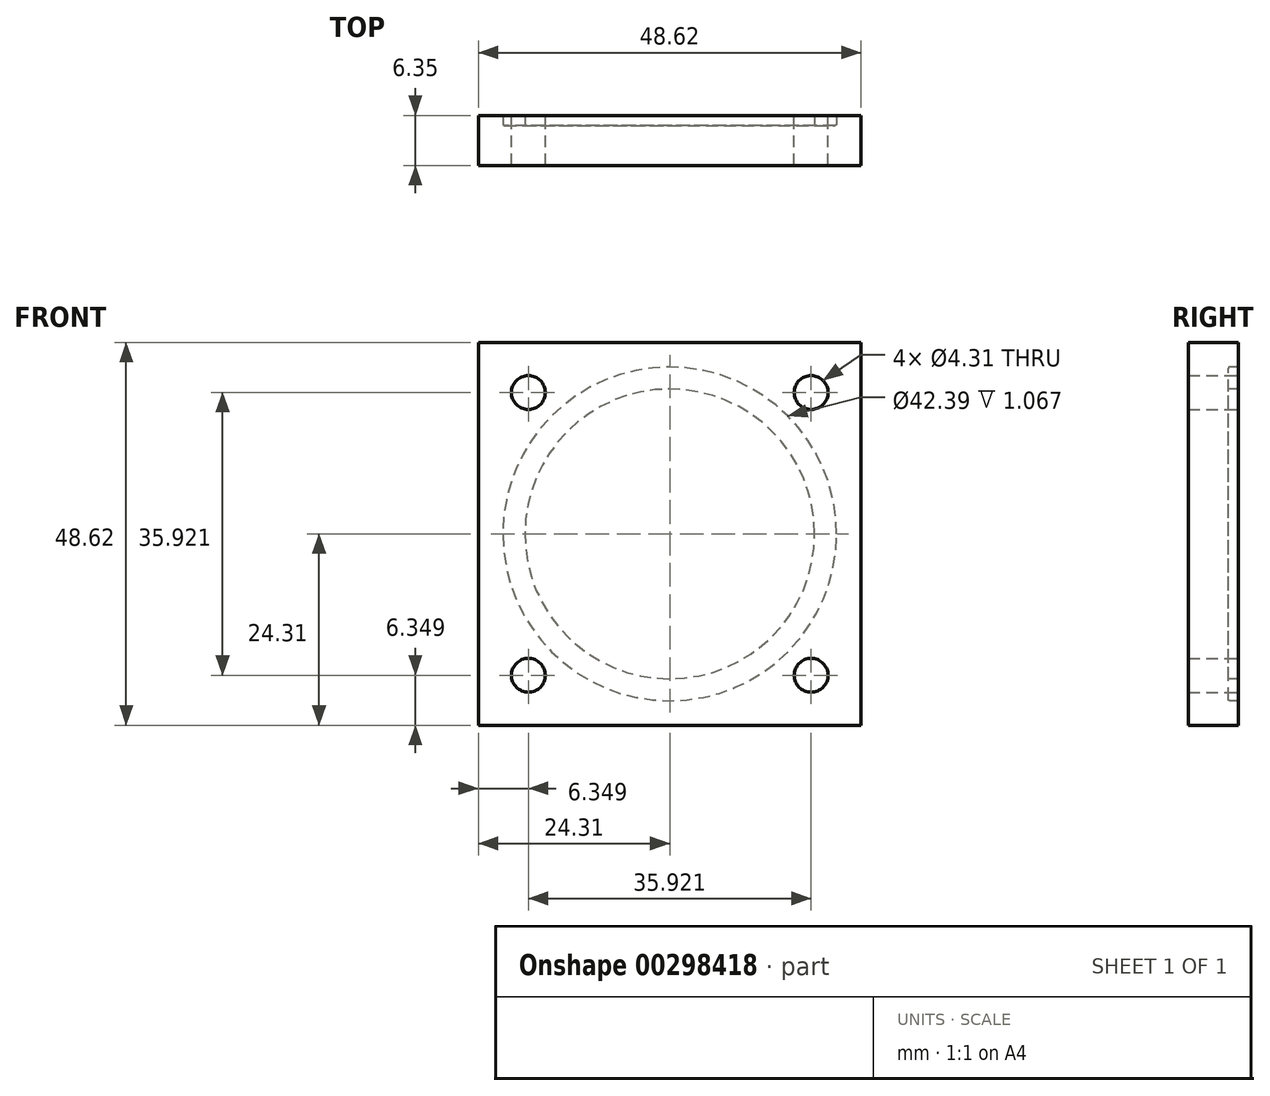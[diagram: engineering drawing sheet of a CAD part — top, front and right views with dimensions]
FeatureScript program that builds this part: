
annotation { "Feature Type Name" : "Feature", "Feature Type Description" : "" }
export const myFeature = defineFeature(function(context is Context, id is Id, definition is map)
    precondition{}
    {
        {
            var Q0;
            Q0=qCreatedBy(makeId("Front.planeOp"),FACE);
            var sketch = newSketch(context, id + "F0", { "sketchPlane" : qUnion([Q0])});
            skLineSegment(sketch, "E0.bottom", {"start": v(24.31, 24.31) * mm, "end": v(-24.31, 24.31) * mm});
            skLineSegment(sketch, "E0.top", {"start": v(24.31, -24.31) * mm, "end": v(-24.31, -24.31) * mm});
            skLineSegment(sketch, "E0.left", {"start": v(24.31, 24.31) * mm, "end": v(24.31, -24.31) * mm});
            skLineSegment(sketch, "E0.right", {"start": v(-24.31, 24.31) * mm, "end": v(-24.31, -24.31) * mm});
            skPoint(sketch, "E0.middle", {"position": v(0, 0) * mm});
            skCircle(sketch, "E1", {"center": v(-17.96, -17.96) * mm, "radius": 2.15 * mm});
            skCircle(sketch, "E2", {"center": v(0, 0) * mm, "radius": 25.4 * mm, "construction": true});
            skLineSegment(sketch, "E3", {"start": v(-17.96, -17.96) * mm, "end": v(0, 0) * mm, "construction": true});
            skCircle(sketch, "E4.1.0", {"center": v(17.96, -17.96) * mm, "radius": 2.15 * mm});
            skCircle(sketch, "E4.2.0", {"center": v(17.96, 17.96) * mm, "radius": 2.15 * mm});
            skCircle(sketch, "E4.3.0", {"center": v(-17.96, 17.96) * mm, "radius": 2.15 * mm});
            skSolve(sketch);
        }
        {
            var Q0;
            Q0=makeQuery(id+"F0.imprint","IMPRINT",FACE,{"disambiguationData":[TD([[makeQuery(id+"F0.imprint","IMPRINT",EDGE,{"derivedFrom":makeQuery(id+"FBOyUSbzv9L5WvW_0.merge.FRwLIMHdycvGu99_1.1.FLy9HZHc7Aeuiqs_1.boolean.opBoolean","COPY",EDGE,{"derivedFrom":makeQuery(id+"FBOyUSbzv9L5WvW_0.merge.FRwLIMHdycvGu99_1.1.FLy9HZHc7Aeuiqs_1.opExtrude","CAP_EDGE",EDGE,{"disambiguationData":[OSD([sQuery(id+"FBOyUSbzv9L5WvW_0.merge.Fd7ioR1l4POb1cx_1.wireOp",EDGE,"KR8DdwEu-s3LD-aGZ0-tnwe-elepxOLVecz2")])],"isStart":true})})}),-1.0]])]});
            var Q1;
            Q1=makeQuery(id+"F0.imprint","IMPRINT",FACE,{"disambiguationData":[TD([[makeQuery(id+"F0.imprint","IMPRINT",EDGE,{"derivedFrom":sQuery(id+"F0.wireOp",EDGE,"E0.bottom")}),1.0]])]});
            extrude(context, id + "F1", {"entities" : qUnion([Q0, Q1]), "depth" : 6.35 * mm});
        }
        {
            var Q0;
            Q0=makeQuery(id+"F1.opExtrude","CAP_EDGE",EDGE,{"disambiguationData":[OSD([sQuery(id+"F0.wireOp",EDGE,"E0.right")])],"isStart":false});
            cPoint(context, id + "F2", {"entities" : qUnion([Q0]), "parameter" : 0.5});
        }
        {
            var Q0;
            Q0=makeQuery(id+"F1.opExtrude","CAP_EDGE",EDGE,{"disambiguationData":[OSD([sQuery(id+"F0.wireOp",EDGE,"E0.left")])],"isStart":false});
            cPoint(context, id + "F3", {"entities" : qUnion([Q0]), "parameter" : 0.5});
        }
        {
            var Q0;
            Q0=makeQuery(id+"F1.opExtrude","CAP_EDGE",EDGE,{"disambiguationData":[OSD([sQuery(id+"F0.wireOp",EDGE,"E0.left")])],"isStart":true});
            cPoint(context, id + "F4", {"entities" : qUnion([Q0]), "parameter" : 0.5});
        }
        {
            var Q0;
            Q0 = qCreatedBy(id + "F2" ,VERTEX);
            var Q1;
            Q1 = qCreatedBy(id + "F3" ,VERTEX);
            var Q2;
            Q2 = qCreatedBy(id + "F4" ,VERTEX);
            cPlane(context, id + "F5", {"entities" : qUnion([Q0, Q1, Q2]), "cplaneType" : CPlaneType.THREE_POINT, "offset" : 25.4 * mm, "width" : 152.4 * mm, "height" : 152.4 * mm});
        }
        {
            var Q0;
            Q0=qCreatedBy(id+"F5.planeOp",FACE);
            var sketch = newSketch(context, id + "F6", { "sketchPlane" : qUnion([Q0])});
            skLineSegment(sketch, "E5.bottom", {"start": v(-18.4, 0) * mm, "end": v(-21.2, 0) * mm});
            skLineSegment(sketch, "E5.top", {"start": v(-18.4, 1.27) * mm, "end": v(-21.2, 1.27) * mm});
            skLineSegment(sketch, "E5.left", {"start": v(-18.4, 0) * mm, "end": v(-18.4, 1.27) * mm});
            skLineSegment(sketch, "E5.right", {"start": v(-21.2, 0) * mm, "end": v(-21.2, 1.27) * mm});
            skPoint(sketch, "E5.middle", {"position": v(-19.8, 0.64) * mm});
            skLineSegment(sketch, "E6", {"start": v(0, -20.02) * mm, "end": v(0, 19.12) * mm, "construction": true});
            skSolve(sketch);
        }
        {
            var Q0;
            Q0 = qSketchRegion(id + "F6", true);
            var Q1;
            Q1=sQuery(id+"F6.wireOp",EDGE,"E6");
            revolve(context, id + "F7", {"operationType" : NewBodyOperationType.REMOVE, "entities" : qUnion([Q0]), "axis" : qUnion([Q1]), "revolveType" : RevolveType.FULL, "oppositeDirection" : true});
        }
        {
            var Q0;
            Q0=makeQuery(id+"F7.boolean.opBoolean","COPY",EDGE,{"derivedFrom":makeQuery(id+"F7.opRevolve","SWEPT_EDGE",EDGE,{"disambiguationData":[OSD([sQuery(id+"F6.wireOp",EDGE,"E5.top"),sQuery(id+"F6.wireOp",EDGE,"E5.right")])]})});
            var Q1;
            Q1=makeQuery(id+"F7.boolean.opBoolean","COPY",EDGE,{"derivedFrom":makeQuery(id+"F7.opRevolve","SWEPT_EDGE",EDGE,{"disambiguationData":[OSD([sQuery(id+"F6.wireOp",EDGE,"E5.bottom"),sQuery(id+"F6.wireOp",EDGE,"E5.left")])]})});
            fillet(context, id + "F8", {"entities" : qUnion([Q0, Q1]), "radius" : 0.2 * mm, "tangentPropagation" : true, "allowEdgeOverflow" : false});
        }
    });
